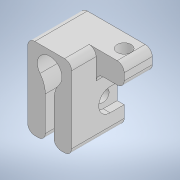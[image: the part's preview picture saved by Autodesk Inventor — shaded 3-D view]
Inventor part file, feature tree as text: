
AUTODESK INVENTOR PART (.ipt)
format: ipt  version: 2022 (Build 260153000, 153)  size: 219,648 bytes
history: native  units: in
note: dims shown in document units (in); Inventor stores cm internally (conversion verified against a paired STEP export)
features: sketch x4, extrude x4, hole x3, projected_geometry x2, plane x1, fillet x1
ambient origin geometry x8: Origin, YZ Plane, XZ Plane, XY Plane, X Axis, Y Axis, Z Axis, Center Point
bodies: Body1 (feature_tree)
feature tree (15):
  sketch  "Sketch14"  dims[d67=0.2756in d68=0.0984in]
  extrude  "Extrusion8"  Depth=0.0984in
  extrude  "Extrusion9"  Depth=0.2756in
  hole  "Hole12"  [1 undecoded]
  plane  "Work Plane4"
  sketch  "Sketch18"  dims[d69=0.2756in d70=0.2756in]
  extrude  "Extrusion13"  Depth=0.1969in
  hole  "Hole16"  [1 undecoded]
  hole  "Hole15"  [1 undecoded]
  extrude  "Extrusion14"  [1 undecoded]
  fillet  "Fillet3"  Radius=0.315in
  sketch  "Sketch19"  dims[d71=0.5906in d72=0.1969in]
  projected_geometry  "Projected Loop2"
  sketch  "Sketch20"  dims[d73=0.1969in d74=0.1969in d75=0.2756in d76=0.0in d77=0.315in d78=0.0in d79=0.1575in d80=0.2362in d81=0.1575in d82=0.0787in d83=90.0deg d84=0.315in d85=0.8108in d111=-0.1181in d112=0.315in d113=0.2165in d116=0.2362in d117=0.0in d126=0.1339in d127=0.2362in d128=0.2559in d129=0.0787in d130=90.0deg d131=0.315in d132=0.8108in d133=0.2362in d134=0.0in d135=0.0787in d139=0.315in d140=0.1575in d141=0.2362in d142=0.1575in d143=0.0787in d144=90.0deg d145=0.315in d146=0.8108in]
  projected_geometry  "Projected Loop3"
note: 4 required parameter values undecoded (feature->parameter linkage not recoverable at this tier; creation-order binding heuristic only, values carry confidence <= 0.55)
